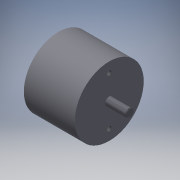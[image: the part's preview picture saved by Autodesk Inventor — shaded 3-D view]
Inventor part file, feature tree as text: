
AUTODESK INVENTOR PART (.ipt)
format: ipt  version: 2018 (Build 220112000, 112)  size: 121,856 bytes
history: native  units: mm
features: revolve x1, hole x1, chamfer x1, sketch x1
ambient origin geometry x8: Origin, YZ Plane, XZ Plane, XY Plane, X Axis, Y Axis, Z Axis, Center Point
bodies: Volumenkörper1 (feature_tree)
feature tree (4):
  revolve  "Umdrehung1"
  hole  "Bohrung1"  [1 undecoded]
  chamfer  "Fase1"  Distance=58.0mm
  sketch  "Skizze2"  dims[d0=15.0mm d2=37.0mm d3=58.0mm d4=25.0mm d5=3.0mm d6=3.0mm d7=90.0deg d8=35.0mm d9=17.5mm d10=3.242mm d11=5.0mm d12=4.0mm d13=2.0mm d14=90.0deg d15=6.0mm d16=20.594885mm d18=0.5mm d19=2.0mm d20=45.0deg]
note: 1 required parameter value undecoded (feature->parameter linkage not recoverable at this tier; creation-order binding heuristic only, values carry confidence <= 0.55)
